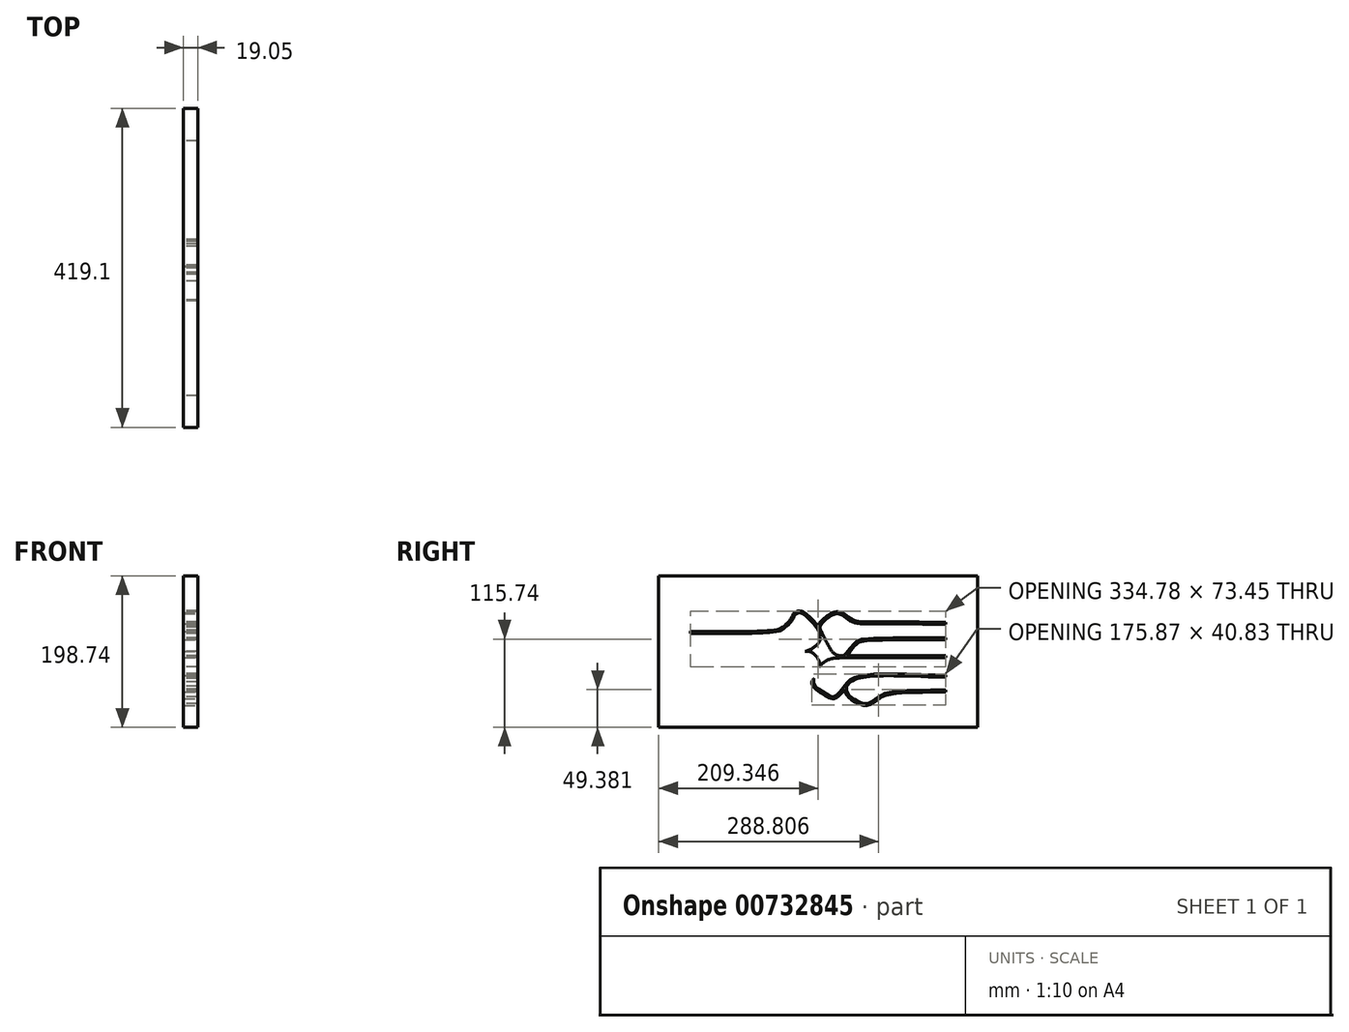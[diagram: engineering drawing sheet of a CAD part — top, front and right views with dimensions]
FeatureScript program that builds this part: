
annotation { "Feature Type Name" : "Feature", "Feature Type Description" : "" }
export const myFeature = defineFeature(function(context is Context, id is Id, definition is map)
    precondition{}
    {
        {
            var Q0;
            Q0=qCreatedBy(makeId("Top.planeOp"),FACE);
            var sketch = newSketch(context, id + "F0", { "sketchPlane" : qUnion([Q0])});
            skLineSegment(sketch, "E0.bottom", {"start": v(-194.14, 91.97) * mm, "end": v(224.96, 91.97) * mm});
            skLineSegment(sketch, "E0.top", {"start": v(-194.14, -106.77) * mm, "end": v(224.96, -106.77) * mm});
            skLineSegment(sketch, "E0.left", {"start": v(-194.14, 91.97) * mm, "end": v(-194.14, -106.77) * mm});
            skLineSegment(sketch, "E0.right", {"start": v(224.96, 91.97) * mm, "end": v(224.96, -106.77) * mm});
            skLineSegment(sketch, "E1", {"start": v(-153.12, 42.36) * mm, "end": v(-153.12, -60.08) * mm, "construction": true});
            skLineSegment(sketch, "E2", {"start": v(182.6, 53.3) * mm, "end": v(182.6, -59.45) * mm, "construction": true});
            skLineSegment(sketch, "E3", {"start": v(-194.14, -84.72) * mm, "end": v(224.96, -84.72) * mm, "construction": true});
            skLineSegment(sketch, "E4", {"start": v(224.96, 74.6) * mm, "end": v(-194.14, 74.6) * mm, "construction": true});
            skFitSpline(sketch, "E5", {"points": [v(-153.12, 42.36) * mm, v(-85.66, 41.43) * mm, v(-61.56, 50.67) * mm, v(-52.92, 59.9) * mm, v(-43.08, 63.12) * mm, v(-26.22, 52.28) * mm, v(-22.4, 42.36) * mm, v(-29.03, 25.17) * mm, v(-52.32, 18.74) * mm, v(-93.08, 17.54) * mm, v(-153.12, 17.94) * mm], "startDerivative": vector(446.25, 0) * mm, "endDerivative": vector(-405.98, 5.29) * mm});
            skFitSpline(sketch, "E6", {"points": [v(-29.03, 25.17) * mm, v(-19.86, 34.51) * mm, v(-15.74, 41.68) * mm, v(-7.3, 44.38) * mm, v(9.73, 30.4) * mm, v(18.56, 16.74) * mm, v(16.76, 3.28) * mm, v(-1.9, -8.46) * mm, v(-28.3, -7.95) * mm, v(-153.12, -9.45) * mm], "startDerivative": vector(129.35, 101.24) * mm, "endDerivative": vector(-596.54, 19.6) * mm});
            skFitSpline(sketch, "E7", {"points": [v(-1.9, -8.46) * mm, v(12.92, -16.12) * mm, v(16.05, -27.34) * mm, v(8.52, -42.1) * mm, v(-3.17, -57.41) * mm, v(-18.8, -67.13) * mm, v(-27.98, -66.28) * mm, v(-38.37, -60.05) * mm, v(-46.75, -57.39) * mm, v(-69.7, -57.84) * mm, v(-153.12, -57.4) * mm], "startDerivative": vector(256.7, 25.98) * mm, "endDerivative": vector(-449.03, 7.68) * mm});
            skFitSpline(sketch, "E8", {"points": [v(-153.12, -33.28) * mm, v(-39.68, -32.56) * mm, v(-26.66, -29.57) * mm, v(-11.86, -10.7) * mm, v(-9.58, -9.25) * mm], "startDerivative": vector(278.75, 3.38) * mm, "endDerivative": vector(24, 6.27) * mm});
            skFitSpline(sketch, "E9", {"points": [v(8.52, -42.1) * mm, v(13.44, -56.28) * mm, v(27.07, -65.22) * mm, v(36.44, -67.92) * mm, v(46.52, -59.4) * mm, v(51.57, -52.47) * mm, v(55.9, -47.47) * mm, v(74.35, -39.95) * mm, v(182.6, -39.66) * mm], "startDerivative": vector(-28.03, -108.1) * mm, "endDerivative": vector(414.6, -6.67) * mm});
            skFitSpline(sketch, "E10", {"points": [v(51.57, -52.47) * mm, v(51.57, -59.12) * mm, v(58.17, -68.34) * mm, v(76.06, -76.86) * mm, v(85.85, -74.6) * mm, v(96.36, -67.07) * mm, v(114.4, -61.53) * mm, v(182.6, -59.45) * mm], "startDerivative": vector(-9.74, -75.42) * mm, "endDerivative": vector(284.67, 0.14) * mm});
            skFitSpline(sketch, "E11", {"points": [v(16.05, -27.34) * mm, v(23.86, -19.25) * mm, v(31.24, -15.98) * mm, v(46.92, -14.32) * mm, v(182.6, -14.14) * mm], "startDerivative": vector(67.03, 106.14) * mm, "endDerivative": vector(304, 2.22) * mm});
            skFitSpline(sketch, "E12", {"points": [v(46.92, -14.32) * mm, v(57.8, -4.62) * mm, v(66.45, 4.6) * mm, v(74.97, 7.59) * mm, v(182.6, 9.3) * mm], "startDerivative": vector(72.04, 8.23) * mm, "endDerivative": vector(274.39, -0.25) * mm});
            skFitSpline(sketch, "E13", {"points": [v(18.56, 16.74) * mm, v(16.47, 24.06) * mm, v(18.56, 29.6) * mm, v(27.55, 37.97) * mm, v(36.5, 42.94) * mm, v(46.15, 42.23) * mm, v(53.4, 37.12) * mm, v(64.32, 31.73) * mm, v(95.14, 30.17) * mm, v(182.6, 29.74) * mm], "startDerivative": vector(-40.2, 100.98) * mm, "endDerivative": vector(378.26, -3.27) * mm});
            skFitSpline(sketch, "E14", {"points": [v(53.4, 37.12) * mm, v(48.66, 44.22) * mm, v(52.3, 56.52) * mm, v(63.9, 64.95) * mm, v(72.28, 67.08) * mm, v(81.36, 62.54) * mm, v(91.59, 56) * mm, v(182.6, 53.3) * mm], "startDerivative": vector(-72.96, 59.52) * mm, "endDerivative": vector(357.02, 12.94) * mm});
            skFitSpline(sketch, "E15", {"points": [v(17.55, 19.29) * mm, v(26.6, 1.96) * mm, v(34.05, -9.78) * mm, v(39.6, -13.31) * mm, v(46.92, -14.32) * mm], "startDerivative": vector(28.44, -55.33) * mm, "endDerivative": vector(53.22, 3.78) * mm});
            skSolve(sketch);
        }
        {
            var Q0;
            Q0=qCreatedBy(makeId("Right.planeOp"),FACE);
            var sketch = newSketch(context, id + "F1", { "sketchPlane" : qUnion([Q0])});
            skLineSegment(sketch, "E16.bottom", {"start": v(-220.53, 98.7) * mm, "end": v(198.57, 98.7) * mm});
            skLineSegment(sketch, "E16.top", {"start": v(-220.53, -100.04) * mm, "end": v(198.57, -100.04) * mm});
            skLineSegment(sketch, "E16.left", {"start": v(-220.53, 98.7) * mm, "end": v(-220.53, -100.04) * mm});
            skLineSegment(sketch, "E16.right", {"start": v(198.57, 98.7) * mm, "end": v(198.57, -100.04) * mm});
            skLineSegment(sketch, "E17", {"start": v(-220.53, -78) * mm, "end": v(198.57, -78) * mm, "construction": true});
            skLineSegment(sketch, "E18", {"start": v(198.57, 81.32) * mm, "end": v(-220.53, 81.32) * mm, "construction": true});
            skFitSpline(sketch, "E19.0", {"points": [v(-179.52, 50.36) * mm, v(-174.85, 50.36) * mm, v(-165.38, 50.12) * mm, v(-151.21, 49.42) * mm, v(-137.52, 48.76) * mm, v(-126.88, 48.56) * mm, v(-119.04, 48.8) * mm, v(-113.57, 49.21) * mm, v(-108.56, 49.92) * mm, v(-104, 50.91) * mm, v(-99.9, 52.15) * mm, v(-96.25, 53.62) * mm, v(-93.03, 55.28) * mm, v(-90.72, 56.8) * mm, v(-89.08, 58.1) * mm, v(-87.58, 59.43) * mm, v(-85.9, 61.17) * mm, v(-84.08, 63.33) * mm, v(-82.3, 65.46) * mm, v(-80.39, 67.47) * mm, v(-78.2, 69.23) * mm, v(-75.7, 70.59) * mm, v(-73.32, 71.22) * mm, v(-71.26, 71.33) * mm, v(-69.64, 71.2) * mm, v(-67.95, 70.84) * mm, v(-65.67, 70.1) * mm, v(-62.78, 68.74) * mm, v(-59.36, 66.63) * mm, v(-56.68, 64.6) * mm, v(-54.71, 62.92) * mm, v(-53.35, 61.64) * mm, v(-52.12, 60.38) * mm, v(-51.03, 59.14) * mm, v(-50.1, 57.92) * mm, v(-49.05, 56.3) * mm, v(-48.1, 54.2) * mm, v(-47.55, 51.48) * mm, v(-47.48, 48.49) * mm, v(-47.82, 45.09) * mm, v(-48.6, 41.47) * mm, v(-49.86, 37.84) * mm, v(-51.34, 34.96) * mm, v(-52.82, 32.85) * mm, v(-54.08, 31.4) * mm, v(-55.5, 30.1) * mm, v(-57.04, 28.99) * mm, v(-58.7, 28.03) * mm, v(-61.06, 26.96) * mm, v(-64.24, 25.96) * mm, v(-68.34, 25.15) * mm, v(-72.68, 24.63) * mm, v(-77.19, 24.3) * mm, v(-81.8, 24.02) * mm, v(-86.52, 23.77) * mm, v(-91.36, 23.57) * mm, v(-98, 23.34) * mm, v(-106.65, 23.13) * mm, v(-117.63, 23) * mm, v(-129.29, 22.96) * mm, v(-141.49, 23) * mm, v(-154.05, 23.1) * mm, v(-166.8, 23.24) * mm, v(-175.3, 23.35) * mm, v(-179.53, 23.4) * mm]});
            skFitSpline(sketch, "E20.0", {"points": [v(-178.58, 47.83) * mm, v(-173.95, 47.83) * mm, v(-164.54, 47.58) * mm, v(-150.4, 46.87) * mm, v(-136.68, 46.2) * mm, v(-125.94, 45.99) * mm, v(-117.98, 46.22) * mm, v(-113.3, 46.57) * mm, v(-109.77, 47) * mm, v(-106.4, 47.55) * mm, v(-100.86, 48.75) * mm, v(-95.4, 50.66) * mm, v(-90.82, 53.03) * mm, v(-88.3, 54.68) * mm, v(-86.5, 56.09) * mm, v(-84.86, 57.55) * mm, v(-83.06, 59.43) * mm, v(-81.18, 61.65) * mm, v(-79.43, 63.72) * mm, v(-77.98, 65.25) * mm, v(-76.76, 66.3) * mm, v(-75.48, 67.24) * mm, v(-73.79, 68.15) * mm, v(-71.95, 68.63) * mm, v(-70.34, 68.72) * mm, v(-69.27, 68.63) * mm, v(-68.37, 68.47) * mm, v(-67.43, 68.24) * mm, v(-66.2, 67.84) * mm, v(-64.64, 67.18) * mm, v(-62.52, 66.1) * mm, v(-59.85, 64.45) * mm, v(-56.8, 62.16) * mm, v(-54.56, 60.14) * mm, v(-53.03, 58.57) * mm, v(-52.05, 57.44) * mm, v(-51.23, 56.37) * mm, v(-50.35, 55) * mm, v(-49.6, 53.32) * mm, v(-49.22, 51.5) * mm, v(-49.12, 49.84) * mm, v(-49.13, 48.46) * mm, v(-49.24, 46.96) * mm, v(-49.51, 44.85) * mm, v(-50.12, 42.08) * mm, v(-51.27, 38.75) * mm, v(-52.6, 36.17) * mm, v(-53.9, 34.33) * mm, v(-54.98, 33.09) * mm, v(-56.17, 32) * mm, v(-57.93, 30.73) * mm, v(-60.44, 29.46) * mm, v(-63.92, 28.35) * mm, v(-67.8, 27.6) * mm, v(-71.99, 27.1) * mm, v(-75.68, 26.82) * mm, v(-78.72, 26.63) * mm, v(-81.8, 26.45) * mm, v(-85.71, 26.25) * mm, v(-90.54, 26.05) * mm, v(-97.15, 25.83) * mm, v(-105.77, 25.63) * mm, v(-114.9, 25.52) * mm, v(-122.54, 25.49) * mm, v(-130.4, 25.48) * mm, v(-140.55, 25.52) * mm, v(-153.1, 25.63) * mm, v(-165.84, 25.78) * mm, v(-174.35, 25.9) * mm, v(-178.58, 25.95) * mm]});
            skFitSpline(sketch, "E21.0", {"points": [v(-54.64, 30.9) * mm, v(-53.96, 31.44) * mm, v(-52.6, 32.54) * mm, v(-50.63, 34.26) * mm, v(-48.78, 36.05) * mm, v(-47.1, 37.9) * mm, v(-45.88, 39.48) * mm, v(-45.05, 40.77) * mm, v(-44.5, 41.73) * mm, v(-44.02, 42.66) * mm, v(-43.44, 43.86) * mm, v(-42.77, 45.26) * mm, v(-42.06, 46.48) * mm, v(-41.4, 47.34) * mm, v(-40.67, 48.13) * mm, v(-39.56, 49.01) * mm, v(-37.97, 49.77) * mm, v(-36.5, 50.08) * mm, v(-35.24, 50.08) * mm, v(-34.26, 49.96) * mm, v(-33.23, 49.68) * mm, v(-32.14, 49.25) * mm, v(-31, 48.67) * mm, v(-29.43, 47.71) * mm, v(-27.4, 46.22) * mm, v(-24.93, 44.06) * mm, v(-22.5, 41.65) * mm, v(-20.13, 39.13) * mm, v(-18.27, 37.03) * mm, v(-16.86, 35.4) * mm, v(-15.53, 33.84) * mm, v(-14, 31.96) * mm, v(-12.38, 29.8) * mm, v(-11.03, 27.7) * mm, v(-9.93, 25.6) * mm, v(-9.1, 23.46) * mm, v(-8.56, 21.24) * mm, v(-8.32, 18.96) * mm, v(-8.42, 16.67) * mm, v(-8.9, 14.38) * mm, v(-9.79, 12.13) * mm, v(-11.14, 9.96) * mm, v(-13, 7.84) * mm, v(-15.26, 5.84) * mm, v(-17.85, 4.02) * mm, v(-20.67, 2.4) * mm, v(-23.63, 1.04) * mm, v(-26.14, 0.16) * mm, v(-28.12, -0.39) * mm, v(-30.07, -0.82) * mm, v(-32.46, -1.15) * mm, v(-35.36, -1.28) * mm, v(-38.38, -1.2) * mm, v(-41.59, -0.98) * mm, v(-45.06, -0.66) * mm, v(-48.87, -0.32) * mm, v(-53.07, 0) * mm, v(-57.75, 0.2) * mm, v(-62.9, 0.27) * mm, v(-68.46, 0.26) * mm, v(-74.45, 0.17) * mm, v(-82.96, -0.04) * mm, v(-94.5, -0.43) * mm, v(-109.66, -0.98) * mm, v(-125.92, -1.49) * mm, v(-148.81, -1.94) * mm, v(-167.07, -1.86) * mm, v(-179.47, -1.45) * mm]});
            skFitSpline(sketch, "E22.0", {"points": [v(-56.2, 32.9) * mm, v(-55.54, 33.42) * mm, v(-54.23, 34.48) * mm, v(-52.34, 36.14) * mm, v(-50.6, 37.83) * mm, v(-49.04, 39.54) * mm, v(-48.05, 40.82) * mm, v(-47.49, 41.67) * mm, v(-47.14, 42.23) * mm, v(-46.57, 43.21) * mm, v(-45.87, 44.65) * mm, v(-45.03, 46.4) * mm, v(-44.2, 47.85) * mm, v(-43.36, 48.97) * mm, v(-42.63, 49.76) * mm, v(-41.8, 50.49) * mm, v(-40.56, 51.35) * mm, v(-38.8, 52.2) * mm, v(-36.8, 52.62) * mm, v(-35.08, 52.63) * mm, v(-33.76, 52.46) * mm, v(-32.41, 52.1) * mm, v(-31.08, 51.56) * mm, v(-29.75, 50.89) * mm, v(-27.98, 49.81) * mm, v(-25.79, 48.19) * mm, v(-23.2, 45.91) * mm, v(-20.67, 43.42) * mm, v(-18.25, 40.84) * mm, v(-15.98, 38.28) * mm, v(-13.9, 35.86) * mm, v(-12, 33.54) * mm, v(-10.3, 31.26) * mm, v(-8.83, 28.98) * mm, v(-7.62, 26.66) * mm, v(-6.68, 24.24) * mm, v(-6.05, 21.7) * mm, v(-5.77, 19.05) * mm, v(-5.88, 16.35) * mm, v(-6.45, 13.65) * mm, v(-7.33, 11.43) * mm, v(-8.3, 9.7) * mm, v(-9.45, 8.02) * mm, v(-11.2, 6.03) * mm, v(-13.69, 3.84) * mm, v(-16.48, 1.87) * mm, v(-19.5, 0.14) * mm, v(-22.67, -1.31) * mm, v(-25.36, -2.26) * mm, v(-27.5, -2.85) * mm, v(-29.62, -3.32) * mm, v(-32.23, -3.68) * mm, v(-36.38, -3.87) * mm, v(-40.63, -3.61) * mm, v(-45.3, -3.19) * mm, v(-49.07, -2.85) * mm, v(-52.53, -2.6) * mm, v(-55.51, -2.45) * mm, v(-58.66, -2.33) * mm, v(-62.9, -2.27) * mm, v(-68.43, -2.28) * mm, v(-74.4, -2.37) * mm, v(-82.87, -2.58) * mm, v(-94.41, -2.97) * mm, v(-109.57, -3.52) * mm, v(-125.85, -4.03) * mm, v(-148.79, -4.49) * mm, v(-167.1, -4.4) * mm, v(-179.55, -4) * mm]});
            skFitSpline(sketch, "E23.0", {"points": [v(-179.53, -25.28) * mm, v(-173.72, -25.2) * mm, v(-162.07, -25.07) * mm, v(-144.82, -24.88) * mm, v(-128.16, -24.72) * mm, v(-112.44, -24.6) * mm, v(-98, -24.5) * mm, v(-85.2, -24.46) * mm, v(-76.2, -24.47) * mm, v(-70.91, -24.5) * mm, v(-68.2, -24.53) * mm, v(-66.34, -24.55) * mm, v(-64.64, -24.58) * mm, v(-62.6, -24.6) * mm, v(-60.44, -24.58) * mm, v(-58.35, -24.34) * mm, v(-56.9, -23.9) * mm, v(-55.8, -23.34) * mm, v(-54.97, -22.8) * mm, v(-54.11, -22.1) * mm, v(-53.2, -21.24) * mm, v(-52.25, -20.2) * mm, v(-50.94, -18.64) * mm, v(-49.26, -16.41) * mm, v(-47.25, -13.52) * mm, v(-45.3, -10.63) * mm, v(-43.5, -7.92) * mm, v(-42.14, -5.98) * mm, v(-41.16, -4.7) * mm, v(-40.47, -3.9) * mm, v(-39.82, -3.27) * mm, v(-39.17, -2.74) * mm, v(-38.51, -2.32) * mm, v(-37.65, -1.87) * mm, v(-37, -1.59) * mm, v(-36.5, -1.36) * mm]});
            skFitSpline(sketch, "E24.0", {"points": [v(-179.53, -27.79) * mm, v(-167.91, -27.65) * mm, v(-150.38, -27.45) * mm, v(-128.17, -27.25) * mm, v(-112.45, -27.12) * mm, v(-98.02, -27.04) * mm, v(-85.24, -27) * mm, v(-76.24, -27) * mm, v(-70.2, -27.05) * mm, v(-66.32, -27.1) * mm, v(-63.1, -27.16) * mm, v(-60.36, -27.12) * mm, v(-57.91, -26.85) * mm, v(-56.01, -26.28) * mm, v(-54.56, -25.55) * mm, v(-53.5, -24.86) * mm, v(-52.46, -24.02) * mm, v(-51.06, -22.68) * mm, v(-49.32, -20.67) * mm, v(-47.22, -17.9) * mm, v(-45.17, -14.96) * mm, v(-43.22, -12.04) * mm, v(-41.72, -9.8) * mm, v(-40.63, -8.22) * mm, v(-39.88, -7.18) * mm, v(-39.2, -6.3) * mm, v(-38.63, -5.65) * mm, v(-38.14, -5.17) * mm, v(-37.7, -4.82) * mm, v(-37.27, -4.54) * mm, v(-36.62, -4.2) * mm, v(-35.98, -3.92) * mm, v(-35.47, -3.68) * mm]});
            skFitSpline(sketch, "E25.0", {"points": [v(-28.17, -2.99) * mm, v(-26.92, -2.86) * mm, v(-24.64, -2.87) * mm, v(-21.84, -3.51) * mm, v(-19.52, -4.66) * mm, v(-17.57, -6.2) * mm, v(-16.19, -7.74) * mm, v(-15.2, -9.06) * mm, v(-14.52, -10.1) * mm, v(-13.88, -11.13) * mm, v(-13.11, -12.5) * mm, v(-12.33, -14.23) * mm, v(-11.7, -16.28) * mm, v(-11.47, -18) * mm, v(-11.48, -19.38) * mm, v(-11.58, -20.43) * mm, v(-11.8, -21.5) * mm, v(-12.22, -23) * mm, v(-12.99, -24.91) * mm, v(-14.23, -27.3) * mm, v(-15.7, -29.76) * mm, v(-17.05, -31.84) * mm, v(-18.16, -33.51) * mm, v(-19.27, -35.19) * mm, v(-20.64, -37.28) * mm, v(-22.29, -39.74) * mm, v(-23.96, -42.15) * mm, v(-25.7, -44.5) * mm, v(-27.57, -46.76) * mm, v(-29.24, -48.58) * mm, v(-30.67, -49.99) * mm, v(-32.17, -51.37) * mm, v(-34.15, -53.01) * mm, v(-36.64, -54.83) * mm, v(-39.16, -56.42) * mm, v(-41.65, -57.74) * mm, v(-43.63, -58.58) * mm, v(-45.13, -59.07) * mm, v(-46.53, -59.44) * mm, v(-48.16, -59.66) * mm, v(-49.97, -59.6) * mm, v(-51.74, -59.23) * mm, v(-53.26, -58.67) * mm, v(-54.53, -58.07) * mm, v(-55.84, -57.37) * mm, v(-57.53, -56.37) * mm, v(-59.6, -55.04) * mm, v(-61.65, -53.7) * mm, v(-63.34, -52.66) * mm, v(-64.66, -51.92) * mm, v(-65.96, -51.26) * mm, v(-67.58, -50.57) * mm, v(-69.56, -49.95) * mm, v(-71.66, -49.53) * mm, v(-73.95, -49.29) * mm, v(-76.46, -49.18) * mm, v(-80.16, -49.18) * mm, v(-84.42, -49.35) * mm, v(-89.35, -49.58) * mm, v(-93.4, -49.75) * mm, v(-97.84, -49.9) * mm, v(-102.68, -50) * mm, v(-107.87, -50.08) * mm, v(-115.23, -50.13) * mm, v(-125.16, -50.13) * mm, v(-138, -50.02) * mm, v(-151.5, -49.85) * mm, v(-165.43, -49.63) * mm, v(-174.81, -49.47) * mm, v(-179.5, -49.4) * mm]});
            skFitSpline(sketch, "E26.0", {"points": [v(-28.43, -0.46) * mm, v(-27.01, -0.31) * mm, v(-24.38, -0.32) * mm, v(-21, -1.1) * mm, v(-18.15, -2.5) * mm, v(-15.8, -4.35) * mm, v(-14.22, -6.12) * mm, v(-13.12, -7.6) * mm, v(-12.38, -8.72) * mm, v(-11.69, -9.85) * mm, v(-10.84, -11.37) * mm, v(-9.96, -13.3) * mm, v(-9.22, -15.72) * mm, v(-8.93, -17.8) * mm, v(-8.94, -19.51) * mm, v(-9.07, -20.8) * mm, v(-9.33, -22.11) * mm, v(-9.82, -23.84) * mm, v(-10.69, -25.99) * mm, v(-12.02, -28.56) * mm, v(-13.55, -31.12) * mm, v(-14.93, -33.23) * mm, v(-16.04, -34.92) * mm, v(-17.15, -36.59) * mm, v(-18.52, -38.67) * mm, v(-20.18, -41.16) * mm, v(-21.9, -43.62) * mm, v(-23.7, -46.05) * mm, v(-25.64, -48.42) * mm, v(-27.75, -50.72) * mm, v(-30.08, -52.93) * mm, v(-32.59, -55.02) * mm, v(-35.2, -56.93) * mm, v(-37.88, -58.61) * mm, v(-40.55, -60.03) * mm, v(-43.16, -61.14) * mm, v(-45.66, -61.88) * mm, v(-48.02, -62.2) * mm, v(-50.28, -62.13) * mm, v(-52.47, -61.67) * mm, v(-54.6, -60.87) * mm, v(-56.75, -59.79) * mm, v(-58.88, -58.51) * mm, v(-60.99, -57.16) * mm, v(-63.03, -55.83) * mm, v(-64.97, -54.63) * mm, v(-66.75, -53.68) * mm, v(-68.46, -52.95) * mm, v(-70.19, -52.42) * mm, v(-72.04, -52.04) * mm, v(-74.13, -51.82) * mm, v(-76.5, -51.71) * mm, v(-80.08, -51.72) * mm, v(-84.3, -51.89) * mm, v(-89.24, -52.11) * mm, v(-93.3, -52.29) * mm, v(-97.78, -52.43) * mm, v(-104.25, -52.58) * mm, v(-113.23, -52.67) * mm, v(-125.17, -52.66) * mm, v(-138.03, -52.56) * mm, v(-156.05, -52.33) * mm, v(-170.18, -52.08) * mm, v(-179.54, -51.92) * mm]});
            skFitSpline(sketch, "E27.0", {"points": [v(23.92, -45.58) * mm, v(23.82, -46.36) * mm, v(23.66, -47.57) * mm, v(23.57, -49.27) * mm, v(23.6, -50.58) * mm, v(23.76, -51.93) * mm, v(24.09, -53.33) * mm, v(24.6, -54.72) * mm, v(25.52, -56.57) * mm, v(26.78, -58.41) * mm, v(28.37, -60.23) * mm, v(29.74, -61.57) * mm, v(31.28, -62.88) * mm, v(33.55, -64.6) * mm, v(36.71, -66.63) * mm, v(40.8, -68.74) * mm, v(44.24, -70.11) * mm, v(46.9, -70.9) * mm, v(48.84, -71.33) * mm, v(50.68, -71.55) * mm, v(53, -71.58) * mm, v(55.66, -71.13) * mm, v(58.06, -70.14) * mm, v(59.9, -69.1) * mm, v(61.7, -67.94) * mm, v(63.92, -66.3) * mm, v(66.15, -64.55) * mm, v(67.97, -63.2) * mm, v(69.36, -62.23) * mm, v(70.76, -61.33) * mm, v(72.69, -60.23) * mm, v(75.24, -59.04) * mm, v(78.7, -57.87) * mm, v(82.72, -56.9) * mm, v(87.4, -56.12) * mm, v(92.93, -55.5) * mm, v(99.21, -55) * mm, v(106.14, -54.63) * mm, v(113.63, -54.37) * mm, v(124.24, -54.13) * mm, v(138.42, -54) * mm, v(150.28, -54) * mm, v(156.2, -54) * mm]});
            skFitSpline(sketch, "E28.0", {"points": [v(26.44, -45.91) * mm, v(26.34, -46.7) * mm, v(26.14, -48.22) * mm, v(26.1, -50.05) * mm, v(26.27, -51.5) * mm, v(26.61, -52.95) * mm, v(27.43, -54.86) * mm, v(28.79, -56.86) * mm, v(30.22, -58.48) * mm, v(31.46, -59.7) * mm, v(32.87, -60.9) * mm, v(34.46, -62.11) * mm, v(36.19, -63.28) * mm, v(38.63, -64.77) * mm, v(41.86, -66.44) * mm, v(45.1, -67.73) * mm, v(47.55, -68.45) * mm, v(49.28, -68.83) * mm, v(50.86, -69.02) * mm, v(52.79, -69.04) * mm, v(54.94, -68.67) * mm, v(56.95, -67.85) * mm, v(58.58, -66.94) * mm, v(60.23, -65.88) * mm, v(62.36, -64.3) * mm, v(65.05, -62.2) * mm, v(67.43, -60.46) * mm, v(69.45, -59.16) * mm, v(71.01, -58.27) * mm, v(72.64, -57.46) * mm, v(74.92, -56.48) * mm, v(78.01, -55.43) * mm, v(82.23, -54.42) * mm, v(87.07, -53.61) * mm, v(92.7, -52.97) * mm, v(99.05, -52.48) * mm, v(106.04, -52.1) * mm, v(113.56, -51.84) * mm, v(124.2, -51.6) * mm, v(138.42, -51.48) * mm, v(150.28, -51.47) * mm, v(156.2, -51.47) * mm]});
            skFitSpline(sketch, "E29.0", {"points": [v(-19.1, -35.06) * mm, v(-19.33, -36.15) * mm, v(-19.64, -38.19) * mm, v(-19.61, -40.9) * mm, v(-19.12, -43.31) * mm, v(-18.22, -45.43) * mm, v(-17, -47.28) * mm, v(-15.53, -48.9) * mm, v(-14.18, -50.14) * mm, v(-13.05, -51.09) * mm, v(-11.87, -52.02) * mm, v(-10.34, -53.15) * mm, v(-8.44, -54.46) * mm, v(-6.5, -55.7) * mm, v(-4.55, -56.9) * mm, v(-2.62, -58.04) * mm, v(-0.75, -59.12) * mm, v(1.04, -60.13) * mm, v(2.79, -61.08) * mm, v(4.53, -61.88) * mm, v(6.3, -62.46) * mm, v(7.85, -62.68) * mm, v(9.12, -62.64) * mm, v(10.08, -62.5) * mm, v(11.04, -62.21) * mm, v(11.97, -61.82) * mm, v(12.88, -61.34) * mm, v(14.07, -60.6) * mm, v(15.5, -59.49) * mm, v(17.14, -57.97) * mm, v(18.69, -56.35) * mm, v(20.12, -54.7) * mm, v(21.41, -53.1) * mm, v(22.55, -51.64) * mm, v(23.57, -50.26) * mm, v(24.8, -48.54) * mm, v(25.87, -46.97) * mm, v(26.9, -45.52) * mm, v(27.67, -44.49) * mm, v(28.5, -43.5) * mm, v(29.42, -42.52) * mm, v(30.5, -41.54) * mm, v(31.78, -40.54) * mm, v(33.28, -39.55) * mm, v(35.6, -38.24) * mm, v(38.45, -37) * mm, v(41.93, -35.88) * mm, v(44.87, -35.11) * mm, v(48.16, -34.45) * mm, v(51.83, -33.9) * mm, v(55.87, -33.44) * mm, v(61.7, -32.97) * mm, v(69.75, -32.6) * mm, v(80.45, -32.47) * mm, v(92.02, -32.57) * mm, v(108.33, -32.92) * mm, v(129.94, -33.63) * mm, v(147.56, -34.12) * mm, v(156.2, -34.27) * mm]});
            skFitSpline(sketch, "E30.0", {"points": [v(-16.65, -35.69) * mm, v(-16.87, -36.67) * mm, v(-17.14, -38.46) * mm, v(-17.1, -40.72) * mm, v(-16.7, -42.63) * mm, v(-16, -44.28) * mm, v(-15.02, -45.77) * mm, v(-13.77, -47.17) * mm, v(-12.54, -48.29) * mm, v(-11.47, -49.18) * mm, v(-10.36, -50.06) * mm, v(-8.9, -51.14) * mm, v(-7.06, -52.4) * mm, v(-5.17, -53.62) * mm, v(-3.27, -54.78) * mm, v(-1.37, -55.9) * mm, v(0.49, -56.96) * mm, v(2.27, -57.97) * mm, v(3.92, -58.87) * mm, v(5.46, -59.57) * mm, v(6.9, -60.03) * mm, v(8, -60.18) * mm, v(8.86, -60.15) * mm, v(9.5, -60.05) * mm, v(10.16, -59.86) * mm, v(10.86, -59.57) * mm, v(11.58, -59.2) * mm, v(12.57, -58.57) * mm, v(13.83, -57.6) * mm, v(15.33, -56.21) * mm, v(16.78, -54.69) * mm, v(18.15, -53.11) * mm, v(19.4, -51.57) * mm, v(20.5, -50.14) * mm, v(21.48, -48.8) * mm, v(22.38, -47.54) * mm, v(23.21, -46.34) * mm, v(24.01, -45.19) * mm, v(24.8, -44.07) * mm, v(25.64, -42.95) * mm, v(26.56, -41.84) * mm, v(27.61, -40.73) * mm, v(28.83, -39.62) * mm, v(30.26, -38.5) * mm, v(31.92, -37.4) * mm, v(34.45, -35.98) * mm, v(37.51, -34.64) * mm, v(41.18, -33.45) * mm, v(44.26, -32.66) * mm, v(47.68, -31.96) * mm, v(51.47, -31.39) * mm, v(55.59, -30.92) * mm, v(61.5, -30.44) * mm, v(69.64, -30.07) * mm, v(80.4, -29.92) * mm, v(92.02, -30) * mm, v(108.36, -30.35) * mm, v(129.99, -31.04) * mm, v(147.58, -31.52) * mm, v(156.2, -31.66) * mm]});
            skFitSpline(sketch, "E31.0", {"points": [v(-9.28, -21.3) * mm, v(-8.6, -20.22) * mm, v(-7.36, -18.4) * mm, v(-5.82, -16.53) * mm, v(-4.72, -15.48) * mm, v(-3.87, -14.83) * mm, v(-3.22, -14.4) * mm, v(-2.66, -14.05) * mm, v(-2.18, -13.78) * mm, v(-1.69, -13.5) * mm, v(-1.04, -13.16) * mm, v(0.03, -12.6) * mm, v(1.44, -11.92) * mm, v(3.22, -11.16) * mm, v(5.05, -10.5) * mm, v(6.9, -10) * mm, v(8.88, -9.6) * mm, v(11.15, -9.32) * mm, v(13.81, -9.1) * mm, v(16.99, -8.96) * mm, v(20.79, -8.86) * mm, v(25.3, -8.79) * mm, v(30.5, -8.73) * mm, v(36.3, -8.7) * mm, v(42.67, -8.68) * mm, v(51.87, -8.67) * mm, v(64.56, -8.7) * mm, v(81.32, -8.74) * mm, v(99.25, -8.78) * mm, v(124.2, -8.8) * mm, v(143.54, -8.76) * mm, v(156.2, -8.66) * mm]});
            skFitSpline(sketch, "E32.0", {"points": [v(-11.41, -19.93) * mm, v(-10.7, -18.8) * mm, v(-9.4, -16.88) * mm, v(-7.7, -14.8) * mm, v(-6.1, -13.3) * mm, v(-4.82, -12.38) * mm, v(-3.8, -11.76) * mm, v(-3.02, -11.33) * mm, v(-2.22, -10.9) * mm, v(-1.1, -10.31) * mm, v(0.4, -9.59) * mm, v(2.3, -8.78) * mm, v(4.3, -8.07) * mm, v(6.33, -7.5) * mm, v(8.5, -7.08) * mm, v(10.92, -6.77) * mm, v(13.69, -6.56) * mm, v(16.92, -6.41) * mm, v(20.75, -6.31) * mm, v(25.3, -6.23) * mm, v(30.5, -6.18) * mm, v(36.3, -6.15) * mm, v(42.68, -6.13) * mm, v(51.89, -6.13) * mm, v(64.58, -6.15) * mm, v(81.35, -6.2) * mm, v(99.27, -6.25) * mm, v(124.22, -6.29) * mm, v(143.55, -6.24) * mm, v(156.2, -6.15) * mm]});
            skFitSpline(sketch, "E33.0", {"points": [v(20.67, -8.86) * mm, v(21.57, -8.75) * mm, v(23.27, -8.24) * mm, v(25.49, -6.8) * mm, v(27.46, -4.95) * mm, v(29.26, -2.83) * mm, v(30.68, -0.96) * mm, v(31.78, 0.5) * mm, v(32.6, 1.58) * mm, v(33.4, 2.62) * mm, v(34.5, 3.96) * mm, v(35.84, 5.53) * mm, v(37.4, 7.23) * mm, v(38.67, 8.47) * mm, v(39.64, 9.35) * mm, v(40.34, 9.94) * mm, v(41.01, 10.47) * mm, v(41.86, 11.08) * mm, v(42.9, 11.67) * mm, v(44.32, 12.23) * mm, v(46.16, 12.69) * mm, v(48.6, 13.07) * mm, v(51.81, 13.4) * mm, v(57.02, 13.79) * mm, v(65.14, 14.17) * mm, v(77.07, 14.47) * mm, v(90.8, 14.66) * mm, v(105.95, 14.76) * mm, v(127.56, 14.8) * mm, v(144.77, 14.77) * mm, v(156.2, 14.76) * mm]});
            skFitSpline(sketch, "E34.0", {"points": [v(20.38, -6.33) * mm, v(20.99, -6.26) * mm, v(22.15, -5.92) * mm, v(23.88, -4.82) * mm, v(25.59, -3.22) * mm, v(27.26, -1.25) * mm, v(28.64, 0.56) * mm, v(29.75, 2.04) * mm, v(30.86, 3.5) * mm, v(32.26, 5.26) * mm, v(33.93, 7.22) * mm, v(35.58, 9) * mm, v(37.18, 10.58) * mm, v(38.48, 11.72) * mm, v(39.48, 12.5) * mm, v(40.48, 13.22) * mm, v(41.8, 13.98) * mm, v(43.58, 14.67) * mm, v(45.69, 15.19) * mm, v(48.3, 15.59) * mm, v(51.6, 15.93) * mm, v(56.88, 16.33) * mm, v(65.06, 16.7) * mm, v(77.02, 17.02) * mm, v(90.77, 17.2) * mm, v(105.94, 17.3) * mm, v(127.56, 17.34) * mm, v(144.78, 17.3) * mm, v(156.2, 17.3) * mm]});
            skFitSpline(sketch, "E35.0", {"points": [v(-7.71, 26.6) * mm, v(-6.53, 24.3) * mm, v(-4.77, 20.9) * mm, v(-2.48, 16.52) * mm, v(-0.78, 13.28) * mm, v(0.9, 10.1) * mm, v(2.55, 6.99) * mm, v(4.17, 4.03) * mm, v(5.52, 1.8) * mm, v(6.6, 0.2) * mm, v(7.41, -0.88) * mm, v(8.23, -1.83) * mm, v(9.04, -2.63) * mm, v(9.86, -3.32) * mm, v(10.7, -3.9) * mm, v(11.53, -4.41) * mm, v(12.38, -4.84) * mm, v(13.24, -5.22) * mm, v(14.1, -5.57) * mm, v(14.91, -5.86) * mm, v(16.03, -6.17) * mm, v(17.61, -6.41) * mm, v(19.38, -6.4) * mm, v(20.44, -6.32) * mm]});
            skFitSpline(sketch, "E36.0", {"points": [v(-6.64, 23.92) * mm, v(-7.06, 24.97) * mm, v(-7.68, 26.52) * mm, v(-8.28, 28.45) * mm, v(-8.52, 29.57) * mm, v(-8.62, 30.4) * mm, v(-8.66, 31.17) * mm, v(-8.57, 32.07) * mm, v(-8.27, 33.11) * mm, v(-7.75, 34.2) * mm, v(-6.98, 35.36) * mm, v(-5.94, 36.63) * mm, v(-4.69, 37.96) * mm, v(-3.27, 39.33) * mm, v(-1.73, 40.7) * mm, v(-0.13, 42.04) * mm, v(1.2, 43.11) * mm, v(2.26, 43.93) * mm, v(3.3, 44.72) * mm, v(4.55, 45.63) * mm, v(6.03, 46.58) * mm, v(7.5, 47.39) * mm, v(8.98, 48.02) * mm, v(10.5, 48.48) * mm, v(12.14, 48.76) * mm, v(13.83, 48.85) * mm, v(15.53, 48.76) * mm, v(17.17, 48.49) * mm, v(18.72, 48.04) * mm, v(20.1, 47.42) * mm, v(21.42, 46.63) * mm, v(22.7, 45.7) * mm, v(23.98, 44.66) * mm, v(25.31, 43.55) * mm, v(26.75, 42.42) * mm, v(28.3, 41.33) * mm, v(30.53, 39.95) * mm, v(33.03, 38.71) * mm, v(35.84, 37.7) * mm, v(38.12, 37.06) * mm, v(40.56, 36.56) * mm, v(44.03, 36.06) * mm, v(48.8, 35.7) * mm, v(55.25, 35.55) * mm, v(62.47, 35.56) * mm, v(70.5, 35.63) * mm, v(79.39, 35.65) * mm, v(92.2, 35.64) * mm, v(109.79, 35.56) * mm, v(132.57, 35.4) * mm, v(148.33, 35.26) * mm, v(156.2, 35.19) * mm]});
            skFitSpline(sketch, "E37.0", {"points": [v(27.75, 44.89) * mm, v(27.03, 45.48) * mm, v(25.72, 46.68) * mm, v(24.53, 48.27) * mm, v(23.87, 49.65) * mm, v(23.59, 50.59) * mm, v(23.44, 51.4) * mm, v(23.35, 52.25) * mm, v(23.34, 53.4) * mm, v(23.5, 54.87) * mm, v(23.94, 56.9) * mm, v(24.7, 58.98) * mm, v(25.78, 60.96) * mm, v(26.72, 62.37) * mm, v(27.8, 63.66) * mm, v(29.4, 65.26) * mm, v(31.66, 67.05) * mm, v(34.1, 68.56) * mm, v(36.07, 69.62) * mm, v(37.5, 70.35) * mm, v(38.9, 71.02) * mm, v(40.2, 71.6) * mm, v(41.43, 72.07) * mm, v(42.6, 72.42) * mm, v(43.72, 72.63) * mm, v(44.83, 72.7) * mm, v(45.94, 72.6) * mm, v(47.14, 72.31) * mm, v(48.38, 71.87) * mm, v(49.65, 71.28) * mm, v(50.92, 70.58) * mm, v(52.17, 69.79) * mm, v(53.16, 69.08) * mm, v(53.93, 68.5) * mm, v(54.66, 67.9) * mm, v(55.56, 67.14) * mm, v(57, 65.88) * mm, v(58.6, 64.6) * mm, v(60.54, 63.4) * mm, v(62.21, 62.54) * mm, v(64.15, 61.75) * mm, v(66.4, 61.05) * mm, v(68.94, 60.44) * mm, v(72.72, 59.73) * mm, v(78.14, 59) * mm, v(85.64, 58.4) * mm, v(96.83, 57.87) * mm, v(112.74, 57.7) * mm, v(133.92, 58.06) * mm, v(148.77, 58.54) * mm, v(156.2, 58.81) * mm]});
            skFitSpline(sketch, "E38.0", {"points": [v(26.28, 42.58) * mm, v(25.49, 43.22) * mm, v(23.99, 44.57) * mm, v(22.49, 46.55) * mm, v(21.61, 48.38) * mm, v(21.16, 49.87) * mm, v(20.92, 51.49) * mm, v(20.91, 53.18) * mm, v(21.1, 54.93) * mm, v(21.6, 57.3) * mm, v(22.47, 59.66) * mm, v(23.69, 61.92) * mm, v(24.76, 63.54) * mm, v(26, 65.04) * mm, v(27.8, 66.85) * mm, v(30.3, 68.8) * mm, v(32.9, 70.43) * mm, v(34.96, 71.55) * mm, v(36.46, 72.3) * mm, v(37.88, 73) * mm, v(39.27, 73.63) * mm, v(40.65, 74.16) * mm, v(42.05, 74.58) * mm, v(43.47, 74.85) * mm, v(44.68, 74.92) * mm, v(45.67, 74.87) * mm, v(46.68, 74.75) * mm, v(47.93, 74.45) * mm, v(49.42, 73.93) * mm, v(51.36, 73.04) * mm, v(53.23, 71.92) * mm, v(54.96, 70.69) * mm, v(56.18, 69.73) * mm, v(57.3, 68.78) * mm, v(58.72, 67.56) * mm, v(60.17, 66.4) * mm, v(61.88, 65.35) * mm, v(63.35, 64.6) * mm, v(64.8, 64.01) * mm, v(66.11, 63.58) * mm, v(67.55, 63.16) * mm, v(69.56, 62.68) * mm, v(73.2, 62) * mm, v(78.49, 61.3) * mm, v(85.89, 60.72) * mm, v(94.21, 60.35) * mm, v(103.32, 60.17) * mm, v(116.34, 60.16) * mm, v(133.94, 60.5) * mm, v(148.77, 61.01) * mm, v(156.2, 61.3) * mm]});
            skFitSpline(sketch, "E39.trimOffspring", {"points": [v(-179.52, 50.36) * mm, v(-174.85, 50.36) * mm, v(-165.38, 50.12) * mm, v(-151.21, 49.42) * mm, v(-137.52, 48.76) * mm, v(-126.88, 48.56) * mm, v(-119.04, 48.8) * mm, v(-113.57, 49.21) * mm, v(-108.56, 49.92) * mm, v(-104, 50.91) * mm, v(-99.9, 52.15) * mm, v(-96.25, 53.62) * mm, v(-93.03, 55.28) * mm, v(-90.72, 56.8) * mm, v(-89.08, 58.1) * mm, v(-87.58, 59.43) * mm, v(-85.9, 61.17) * mm, v(-84.08, 63.33) * mm, v(-82.3, 65.46) * mm, v(-80.39, 67.47) * mm, v(-78.2, 69.23) * mm, v(-75.7, 70.59) * mm, v(-73.32, 71.22) * mm, v(-71.26, 71.33) * mm, v(-69.64, 71.2) * mm, v(-67.95, 70.84) * mm, v(-65.67, 70.1) * mm, v(-62.78, 68.74) * mm, v(-59.36, 66.63) * mm, v(-56.68, 64.6) * mm, v(-54.71, 62.92) * mm, v(-53.35, 61.64) * mm, v(-52.12, 60.38) * mm, v(-51.03, 59.14) * mm, v(-50.1, 57.92) * mm, v(-49.05, 56.3) * mm, v(-48.1, 54.2) * mm, v(-47.55, 51.48) * mm, v(-47.48, 48.49) * mm, v(-47.82, 45.09) * mm, v(-48.6, 41.47) * mm, v(-49.86, 37.84) * mm, v(-51.34, 34.96) * mm, v(-52.82, 32.85) * mm, v(-54.08, 31.4) * mm, v(-55.5, 30.1) * mm, v(-57.04, 28.99) * mm, v(-58.7, 28.03) * mm, v(-61.06, 26.96) * mm, v(-64.24, 25.96) * mm, v(-68.34, 25.15) * mm, v(-72.68, 24.63) * mm, v(-77.19, 24.3) * mm, v(-81.8, 24.02) * mm, v(-86.52, 23.77) * mm, v(-91.36, 23.57) * mm, v(-98, 23.34) * mm, v(-106.65, 23.13) * mm, v(-117.63, 23) * mm, v(-129.29, 22.96) * mm, v(-141.49, 23) * mm, v(-154.05, 23.1) * mm, v(-166.8, 23.24) * mm, v(-175.3, 23.35) * mm, v(-179.53, 23.4) * mm]});
            skFitSpline(sketch, "E40.trimOffspring", {"points": [v(-56.2, 32.9) * mm, v(-55.54, 33.42) * mm, v(-54.23, 34.48) * mm, v(-52.34, 36.14) * mm, v(-50.6, 37.83) * mm, v(-49.04, 39.54) * mm, v(-48.05, 40.82) * mm, v(-47.49, 41.67) * mm, v(-47.14, 42.23) * mm, v(-46.57, 43.21) * mm, v(-45.87, 44.65) * mm, v(-45.03, 46.4) * mm, v(-44.2, 47.85) * mm, v(-43.36, 48.97) * mm, v(-42.63, 49.76) * mm, v(-41.8, 50.49) * mm, v(-40.56, 51.35) * mm, v(-38.8, 52.2) * mm, v(-36.8, 52.62) * mm, v(-35.08, 52.63) * mm, v(-33.76, 52.46) * mm, v(-32.41, 52.1) * mm, v(-31.08, 51.56) * mm, v(-29.75, 50.89) * mm, v(-27.98, 49.81) * mm, v(-25.79, 48.19) * mm, v(-23.2, 45.91) * mm, v(-20.67, 43.42) * mm, v(-18.25, 40.84) * mm, v(-15.98, 38.28) * mm, v(-13.9, 35.86) * mm, v(-12, 33.54) * mm, v(-10.3, 31.26) * mm, v(-8.83, 28.98) * mm, v(-7.62, 26.66) * mm, v(-6.68, 24.24) * mm, v(-6.05, 21.7) * mm, v(-5.77, 19.05) * mm, v(-5.88, 16.35) * mm, v(-6.45, 13.65) * mm, v(-7.33, 11.43) * mm, v(-8.3, 9.7) * mm, v(-9.45, 8.02) * mm, v(-11.2, 6.03) * mm, v(-13.69, 3.84) * mm, v(-16.48, 1.87) * mm, v(-19.5, 0.14) * mm, v(-22.67, -1.31) * mm, v(-25.36, -2.26) * mm, v(-27.5, -2.85) * mm, v(-29.62, -3.32) * mm, v(-32.23, -3.68) * mm, v(-36.38, -3.87) * mm, v(-40.63, -3.61) * mm, v(-45.3, -3.19) * mm, v(-49.07, -2.85) * mm, v(-52.53, -2.6) * mm, v(-55.51, -2.45) * mm, v(-58.66, -2.33) * mm, v(-62.9, -2.27) * mm, v(-68.43, -2.28) * mm, v(-74.4, -2.37) * mm, v(-82.87, -2.58) * mm, v(-94.41, -2.97) * mm, v(-109.57, -3.52) * mm, v(-125.85, -4.03) * mm, v(-148.79, -4.49) * mm, v(-167.1, -4.4) * mm, v(-179.55, -4) * mm]});
            skFitSpline(sketch, "E41.trimOffspring", {"points": [v(-56.2, 32.9) * mm, v(-55.54, 33.42) * mm, v(-54.23, 34.48) * mm, v(-52.34, 36.14) * mm, v(-50.6, 37.83) * mm, v(-49.04, 39.54) * mm, v(-48.05, 40.82) * mm, v(-47.49, 41.67) * mm, v(-47.14, 42.23) * mm, v(-46.57, 43.21) * mm, v(-45.87, 44.65) * mm, v(-45.03, 46.4) * mm, v(-44.2, 47.85) * mm, v(-43.36, 48.97) * mm, v(-42.63, 49.76) * mm, v(-41.8, 50.49) * mm, v(-40.56, 51.35) * mm, v(-38.8, 52.2) * mm, v(-36.8, 52.62) * mm, v(-35.08, 52.63) * mm, v(-33.76, 52.46) * mm, v(-32.41, 52.1) * mm, v(-31.08, 51.56) * mm, v(-29.75, 50.89) * mm, v(-27.98, 49.81) * mm, v(-25.79, 48.19) * mm, v(-23.2, 45.91) * mm, v(-20.67, 43.42) * mm, v(-18.25, 40.84) * mm, v(-15.98, 38.28) * mm, v(-13.9, 35.86) * mm, v(-12, 33.54) * mm, v(-10.3, 31.26) * mm, v(-8.83, 28.98) * mm, v(-7.62, 26.66) * mm, v(-6.68, 24.24) * mm, v(-6.05, 21.7) * mm, v(-5.77, 19.05) * mm, v(-5.88, 16.35) * mm, v(-6.45, 13.65) * mm, v(-7.33, 11.43) * mm, v(-8.3, 9.7) * mm, v(-9.45, 8.02) * mm, v(-11.2, 6.03) * mm, v(-13.69, 3.84) * mm, v(-16.48, 1.87) * mm, v(-19.5, 0.14) * mm, v(-22.67, -1.31) * mm, v(-25.36, -2.26) * mm, v(-27.5, -2.85) * mm, v(-29.62, -3.32) * mm, v(-32.23, -3.68) * mm, v(-36.38, -3.87) * mm, v(-40.63, -3.61) * mm, v(-45.3, -3.19) * mm, v(-49.07, -2.85) * mm, v(-52.53, -2.6) * mm, v(-55.51, -2.45) * mm, v(-58.66, -2.33) * mm, v(-62.9, -2.27) * mm, v(-68.43, -2.28) * mm, v(-74.4, -2.37) * mm, v(-82.87, -2.58) * mm, v(-94.41, -2.97) * mm, v(-109.57, -3.52) * mm, v(-125.85, -4.03) * mm, v(-148.79, -4.49) * mm, v(-167.1, -4.4) * mm, v(-179.55, -4) * mm]});
            skFitSpline(sketch, "E42.trimOffspring", {"points": [v(-28.43, -0.46) * mm, v(-27.01, -0.31) * mm, v(-24.38, -0.32) * mm, v(-21, -1.1) * mm, v(-18.15, -2.5) * mm, v(-15.8, -4.35) * mm, v(-14.22, -6.12) * mm, v(-13.12, -7.6) * mm, v(-12.38, -8.72) * mm, v(-11.69, -9.85) * mm, v(-10.84, -11.37) * mm, v(-9.96, -13.3) * mm, v(-9.22, -15.72) * mm, v(-8.93, -17.8) * mm, v(-8.94, -19.51) * mm, v(-9.07, -20.8) * mm, v(-9.33, -22.11) * mm, v(-9.82, -23.84) * mm, v(-10.69, -25.99) * mm, v(-12.02, -28.56) * mm, v(-13.55, -31.12) * mm, v(-14.93, -33.23) * mm, v(-16.04, -34.92) * mm, v(-17.15, -36.59) * mm, v(-18.52, -38.67) * mm, v(-20.18, -41.16) * mm, v(-21.9, -43.62) * mm, v(-23.7, -46.05) * mm, v(-25.64, -48.42) * mm, v(-27.75, -50.72) * mm, v(-30.08, -52.93) * mm, v(-32.59, -55.02) * mm, v(-35.2, -56.93) * mm, v(-37.88, -58.61) * mm, v(-40.55, -60.03) * mm, v(-43.16, -61.14) * mm, v(-45.66, -61.88) * mm, v(-48.02, -62.2) * mm, v(-50.28, -62.13) * mm, v(-52.47, -61.67) * mm, v(-54.6, -60.87) * mm, v(-56.75, -59.79) * mm, v(-58.88, -58.51) * mm, v(-60.99, -57.16) * mm, v(-63.03, -55.83) * mm, v(-64.97, -54.63) * mm, v(-66.75, -53.68) * mm, v(-68.46, -52.95) * mm, v(-70.19, -52.42) * mm, v(-72.04, -52.04) * mm, v(-74.13, -51.82) * mm, v(-76.5, -51.71) * mm, v(-80.08, -51.72) * mm, v(-84.3, -51.89) * mm, v(-89.24, -52.11) * mm, v(-93.3, -52.29) * mm, v(-97.78, -52.43) * mm, v(-104.25, -52.58) * mm, v(-113.23, -52.67) * mm, v(-125.17, -52.66) * mm, v(-138.03, -52.56) * mm, v(-156.05, -52.33) * mm, v(-170.18, -52.08) * mm, v(-179.54, -51.92) * mm]});
            skFitSpline(sketch, "E43.trimOffspring", {"points": [v(-28.43, -0.46) * mm, v(-27.01, -0.31) * mm, v(-24.38, -0.32) * mm, v(-21, -1.1) * mm, v(-18.15, -2.5) * mm, v(-15.8, -4.35) * mm, v(-14.22, -6.12) * mm, v(-13.12, -7.6) * mm, v(-12.38, -8.72) * mm, v(-11.69, -9.85) * mm, v(-10.84, -11.37) * mm, v(-9.96, -13.3) * mm, v(-9.22, -15.72) * mm, v(-8.93, -17.8) * mm, v(-8.94, -19.51) * mm, v(-9.07, -20.8) * mm, v(-9.33, -22.11) * mm, v(-9.82, -23.84) * mm, v(-10.69, -25.99) * mm, v(-12.02, -28.56) * mm, v(-13.55, -31.12) * mm, v(-14.93, -33.23) * mm, v(-16.04, -34.92) * mm, v(-17.15, -36.59) * mm, v(-18.52, -38.67) * mm, v(-20.18, -41.16) * mm, v(-21.9, -43.62) * mm, v(-23.7, -46.05) * mm, v(-25.64, -48.42) * mm, v(-27.75, -50.72) * mm, v(-30.08, -52.93) * mm, v(-32.59, -55.02) * mm, v(-35.2, -56.93) * mm, v(-37.88, -58.61) * mm, v(-40.55, -60.03) * mm, v(-43.16, -61.14) * mm, v(-45.66, -61.88) * mm, v(-48.02, -62.2) * mm, v(-50.28, -62.13) * mm, v(-52.47, -61.67) * mm, v(-54.6, -60.87) * mm, v(-56.75, -59.79) * mm, v(-58.88, -58.51) * mm, v(-60.99, -57.16) * mm, v(-63.03, -55.83) * mm, v(-64.97, -54.63) * mm, v(-66.75, -53.68) * mm, v(-68.46, -52.95) * mm, v(-70.19, -52.42) * mm, v(-72.04, -52.04) * mm, v(-74.13, -51.82) * mm, v(-76.5, -51.71) * mm, v(-80.08, -51.72) * mm, v(-84.3, -51.89) * mm, v(-89.24, -52.11) * mm, v(-93.3, -52.29) * mm, v(-97.78, -52.43) * mm, v(-104.25, -52.58) * mm, v(-113.23, -52.67) * mm, v(-125.17, -52.66) * mm, v(-138.03, -52.56) * mm, v(-156.05, -52.33) * mm, v(-170.18, -52.08) * mm, v(-179.54, -51.92) * mm]});
            skFitSpline(sketch, "E44.trimOffspring", {"points": [v(-9.02, 23.02) * mm, v(-9.44, 24.07) * mm, v(-10.08, 25.67) * mm, v(-10.75, 27.81) * mm, v(-11.05, 29.15) * mm, v(-11.18, 30.21) * mm, v(-11.23, 31.28) * mm, v(-11.1, 32.58) * mm, v(-10.67, 34.08) * mm, v(-9.97, 35.52) * mm, v(-9.03, 36.93) * mm, v(-7.86, 38.35) * mm, v(-6.5, 39.8) * mm, v(-5.01, 41.23) * mm, v(-3.41, 42.66) * mm, v(-1.77, 44.04) * mm, v(-0.11, 45.36) * mm, v(1.5, 46.6) * mm, v(3.08, 47.76) * mm, v(4.7, 48.8) * mm, v(6.35, 49.7) * mm, v(8.08, 50.45) * mm, v(9.91, 51) * mm, v(11.84, 51.33) * mm, v(13.8, 51.43) * mm, v(15.78, 51.33) * mm, v(17.7, 51) * mm, v(19.25, 50.56) * mm, v(20.42, 50.09) * mm, v(21.53, 49.55) * mm, v(22.82, 48.77) * mm, v(24.23, 47.74) * mm, v(25.58, 46.65) * mm, v(26.9, 45.55) * mm, v(28.25, 44.5) * mm, v(29.68, 43.49) * mm, v(31.73, 42.22) * mm, v(34.02, 41.09) * mm, v(36.6, 40.16) * mm, v(38.68, 39.57) * mm, v(40.96, 39.1) * mm, v(44.27, 38.63) * mm, v(48.89, 38.28) * mm, v(55.24, 38.13) * mm, v(61.23, 38.14) * mm, v(66.45, 38.18) * mm, v(71.96, 38.21) * mm, v(79.36, 38.23) * mm, v(88.98, 38.22) * mm, v(99.22, 38.19) * mm, v(113.58, 38.11) * mm, v(132.57, 37.97) * mm, v(148.33, 37.84) * mm, v(156.2, 37.77) * mm]});
            skFitSpline(sketch, "E45.trimOffspring", {"points": [v(-9.97, 25.44) * mm, v(-8.79, 23.13) * mm, v(-7.03, 19.74) * mm, v(-4.73, 15.34) * mm, v(-3.03, 12.1) * mm, v(-1.63, 9.45) * mm, v(-0.52, 7.36) * mm, v(0.58, 5.3) * mm, v(1.96, 2.77) * mm, v(3.37, 0.44) * mm, v(4.53, -1.27) * mm, v(5.43, -2.46) * mm, v(6.35, -3.55) * mm, v(7.32, -4.51) * mm, v(8.31, -5.34) * mm, v(9.3, -6.04) * mm, v(10.3, -6.63) * mm, v(11.29, -7.14) * mm, v(12.25, -7.57) * mm, v(13.18, -7.94) * mm, v(14.14, -8.28) * mm, v(15.17, -8.57) * mm, v(16.3, -8.78) * mm, v(17.98, -8.95) * mm, v(19.47, -8.94) * mm, v(20.62, -8.86) * mm]});
            skFitSpline(sketch, "E46.trimOffspring", {"points": [v(-56.2, 32.9) * mm, v(-55.54, 33.42) * mm, v(-54.23, 34.48) * mm, v(-52.34, 36.14) * mm, v(-50.6, 37.83) * mm, v(-49.04, 39.54) * mm, v(-48.05, 40.82) * mm, v(-47.49, 41.67) * mm, v(-47.14, 42.23) * mm, v(-46.57, 43.21) * mm, v(-45.87, 44.65) * mm, v(-45.03, 46.4) * mm, v(-44.2, 47.85) * mm, v(-43.36, 48.97) * mm, v(-42.63, 49.76) * mm, v(-41.8, 50.49) * mm, v(-40.56, 51.35) * mm, v(-38.8, 52.2) * mm, v(-36.8, 52.62) * mm, v(-35.08, 52.63) * mm, v(-33.76, 52.46) * mm, v(-32.41, 52.1) * mm, v(-31.08, 51.56) * mm, v(-29.75, 50.89) * mm, v(-27.98, 49.81) * mm, v(-25.79, 48.19) * mm, v(-23.2, 45.91) * mm, v(-20.67, 43.42) * mm, v(-18.25, 40.84) * mm, v(-15.98, 38.28) * mm, v(-13.9, 35.86) * mm, v(-12, 33.54) * mm, v(-10.3, 31.26) * mm, v(-8.83, 28.98) * mm, v(-7.62, 26.66) * mm, v(-6.68, 24.24) * mm, v(-6.05, 21.7) * mm, v(-5.77, 19.05) * mm, v(-5.88, 16.35) * mm, v(-6.45, 13.65) * mm, v(-7.33, 11.43) * mm, v(-8.3, 9.7) * mm, v(-9.45, 8.02) * mm, v(-11.2, 6.03) * mm, v(-13.69, 3.84) * mm, v(-16.48, 1.87) * mm, v(-19.5, 0.14) * mm, v(-22.67, -1.31) * mm, v(-25.36, -2.26) * mm, v(-27.5, -2.85) * mm, v(-29.62, -3.32) * mm, v(-32.23, -3.68) * mm, v(-36.38, -3.87) * mm, v(-40.63, -3.61) * mm, v(-45.3, -3.19) * mm, v(-49.07, -2.85) * mm, v(-52.53, -2.6) * mm, v(-55.51, -2.45) * mm, v(-58.66, -2.33) * mm, v(-62.9, -2.27) * mm, v(-68.43, -2.28) * mm, v(-74.4, -2.37) * mm, v(-82.87, -2.58) * mm, v(-94.41, -2.97) * mm, v(-109.57, -3.52) * mm, v(-125.85, -4.03) * mm, v(-148.79, -4.49) * mm, v(-167.1, -4.4) * mm, v(-179.55, -4) * mm]});
            skFitSpline(sketch, "E47.trimOffspring", {"points": [v(-11.41, -19.93) * mm, v(-10.7, -18.8) * mm, v(-9.4, -16.88) * mm, v(-7.7, -14.8) * mm, v(-6.1, -13.3) * mm, v(-4.82, -12.38) * mm, v(-3.8, -11.76) * mm, v(-3.02, -11.33) * mm, v(-2.22, -10.9) * mm, v(-1.1, -10.31) * mm, v(0.4, -9.59) * mm, v(2.3, -8.78) * mm, v(4.3, -8.07) * mm, v(6.33, -7.5) * mm, v(8.5, -7.08) * mm, v(10.92, -6.77) * mm, v(13.69, -6.56) * mm, v(16.92, -6.41) * mm, v(20.75, -6.31) * mm, v(25.3, -6.23) * mm, v(30.5, -6.18) * mm, v(36.3, -6.15) * mm, v(42.68, -6.13) * mm, v(51.89, -6.13) * mm, v(64.58, -6.15) * mm, v(81.35, -6.2) * mm, v(99.27, -6.25) * mm, v(124.22, -6.29) * mm, v(143.55, -6.24) * mm, v(156.2, -6.15) * mm]});
            skFitSpline(sketch, "E48.trimOffspring", {"points": [v(-11.41, -19.93) * mm, v(-10.7, -18.8) * mm, v(-9.4, -16.88) * mm, v(-7.7, -14.8) * mm, v(-6.1, -13.3) * mm, v(-4.82, -12.38) * mm, v(-3.8, -11.76) * mm, v(-3.02, -11.33) * mm, v(-2.22, -10.9) * mm, v(-1.1, -10.31) * mm, v(0.4, -9.59) * mm, v(2.3, -8.78) * mm, v(4.3, -8.07) * mm, v(6.33, -7.5) * mm, v(8.5, -7.08) * mm, v(10.92, -6.77) * mm, v(13.69, -6.56) * mm, v(16.92, -6.41) * mm, v(20.75, -6.31) * mm, v(25.3, -6.23) * mm, v(30.5, -6.18) * mm, v(36.3, -6.15) * mm, v(42.68, -6.13) * mm, v(51.89, -6.13) * mm, v(64.58, -6.15) * mm, v(81.35, -6.2) * mm, v(99.27, -6.25) * mm, v(124.22, -6.29) * mm, v(143.55, -6.24) * mm, v(156.2, -6.15) * mm]});
            skFitSpline(sketch, "E49.trimOffspring", {"points": [v(-19.1, -35.06) * mm, v(-19.33, -36.15) * mm, v(-19.64, -38.19) * mm, v(-19.61, -40.9) * mm, v(-19.12, -43.31) * mm, v(-18.22, -45.43) * mm, v(-17, -47.28) * mm, v(-15.53, -48.9) * mm, v(-14.18, -50.14) * mm, v(-13.05, -51.09) * mm, v(-11.87, -52.02) * mm, v(-10.34, -53.15) * mm, v(-8.44, -54.46) * mm, v(-6.5, -55.7) * mm, v(-4.55, -56.9) * mm, v(-2.62, -58.04) * mm, v(-0.75, -59.12) * mm, v(1.04, -60.13) * mm, v(2.79, -61.08) * mm, v(4.53, -61.88) * mm, v(6.3, -62.46) * mm, v(7.85, -62.68) * mm, v(9.12, -62.64) * mm, v(10.08, -62.5) * mm, v(11.04, -62.21) * mm, v(11.97, -61.82) * mm, v(12.88, -61.34) * mm, v(14.07, -60.6) * mm, v(15.5, -59.49) * mm, v(17.14, -57.97) * mm, v(18.69, -56.35) * mm, v(20.12, -54.7) * mm, v(21.41, -53.1) * mm, v(22.55, -51.64) * mm, v(23.57, -50.26) * mm, v(24.8, -48.54) * mm, v(25.87, -46.97) * mm, v(26.9, -45.52) * mm, v(27.67, -44.49) * mm, v(28.5, -43.5) * mm, v(29.42, -42.52) * mm, v(30.5, -41.54) * mm, v(31.78, -40.54) * mm, v(33.28, -39.55) * mm, v(35.6, -38.24) * mm, v(38.45, -37) * mm, v(41.93, -35.88) * mm, v(44.87, -35.11) * mm, v(48.16, -34.45) * mm, v(51.83, -33.9) * mm, v(55.87, -33.44) * mm, v(61.7, -32.97) * mm, v(69.75, -32.6) * mm, v(80.45, -32.47) * mm, v(92.02, -32.57) * mm, v(108.33, -32.92) * mm, v(129.94, -33.63) * mm, v(147.56, -34.12) * mm, v(156.2, -34.27) * mm]});
            skFitSpline(sketch, "E50.trimOffspring", {"points": [v(-9.02, 23.02) * mm, v(-9.44, 24.07) * mm, v(-10.08, 25.67) * mm, v(-10.75, 27.81) * mm, v(-11.05, 29.15) * mm, v(-11.18, 30.21) * mm, v(-11.23, 31.28) * mm, v(-11.1, 32.58) * mm, v(-10.67, 34.08) * mm, v(-9.97, 35.52) * mm, v(-9.03, 36.93) * mm, v(-7.86, 38.35) * mm, v(-6.5, 39.8) * mm, v(-5.01, 41.23) * mm, v(-3.41, 42.66) * mm, v(-1.77, 44.04) * mm, v(-0.11, 45.36) * mm, v(1.5, 46.6) * mm, v(3.08, 47.76) * mm, v(4.7, 48.8) * mm, v(6.35, 49.7) * mm, v(8.08, 50.45) * mm, v(9.91, 51) * mm, v(11.84, 51.33) * mm, v(13.8, 51.43) * mm, v(15.78, 51.33) * mm, v(17.7, 51) * mm, v(19.25, 50.56) * mm, v(20.42, 50.09) * mm, v(21.53, 49.55) * mm, v(22.82, 48.77) * mm, v(24.23, 47.74) * mm, v(25.58, 46.65) * mm, v(26.9, 45.55) * mm, v(28.25, 44.5) * mm, v(29.68, 43.49) * mm, v(31.73, 42.22) * mm, v(34.02, 41.09) * mm, v(36.6, 40.16) * mm, v(38.68, 39.57) * mm, v(40.96, 39.1) * mm, v(44.27, 38.63) * mm, v(48.89, 38.28) * mm, v(55.24, 38.13) * mm, v(61.23, 38.14) * mm, v(66.45, 38.18) * mm, v(71.96, 38.21) * mm, v(79.36, 38.23) * mm, v(88.98, 38.22) * mm, v(99.22, 38.19) * mm, v(113.58, 38.11) * mm, v(132.57, 37.97) * mm, v(148.33, 37.84) * mm, v(156.2, 37.77) * mm]});
            skLineSegment(sketch, "E51", {"start": v(-178.58, -51.94) * mm, "end": v(-178.58, -49.4) * mm});
            skLineSegment(sketch, "E52", {"start": v(-178.58, -27.78) * mm, "end": v(-178.58, -25.26) * mm});
            skLineSegment(sketch, "E53", {"start": v(-178.58, -4.03) * mm, "end": v(-178.58, -1.48) * mm});
            skLineSegment(sketch, "E54", {"start": v(-178.58, 23.39) * mm, "end": v(-178.58, 25.95) * mm});
            skLineSegment(sketch, "E55", {"start": v(-178.58, 47.83) * mm, "end": v(-178.58, 50.36) * mm});
            skLineSegment(sketch, "E56", {"start": v(156.2, 61.3) * mm, "end": v(156.2, 58.81) * mm});
            skLineSegment(sketch, "E57", {"start": v(156.2, 37.77) * mm, "end": v(156.2, 35.19) * mm});
            skLineSegment(sketch, "E58", {"start": v(156.2, 17.3) * mm, "end": v(156.2, 14.76) * mm});
            skLineSegment(sketch, "E59", {"start": v(156.2, -6.15) * mm, "end": v(156.2, -8.66) * mm});
            skLineSegment(sketch, "E60", {"start": v(156.2, -31.66) * mm, "end": v(156.2, -34.27) * mm});
            skLineSegment(sketch, "E61", {"start": v(156.2, -51.47) * mm, "end": v(156.2, -54) * mm});
            skLineSegment(sketch, "E62", {"start": v(-7.76, 26.85) * mm, "end": v(-7.3, 25.78) * mm});
            skSolve(sketch);
        }
        {
            var Q0;
            Q0=makeQuery(id+"F1.imprint","IMPRINT",FACE,{"disambiguationData":[TD([[makeQuery(id+"F1.imprint","IMPRINT",EDGE,{"derivedFrom":sQuery(id+"F1.wireOp",EDGE,"E16.bottom")}),-1.0]])]});
            extrude(context, id + "F2", {"entities" : qUnion([Q0]), "depth" : 19.05 * mm, "offsetDistance" : 25.4 * mm});
        }
    });
